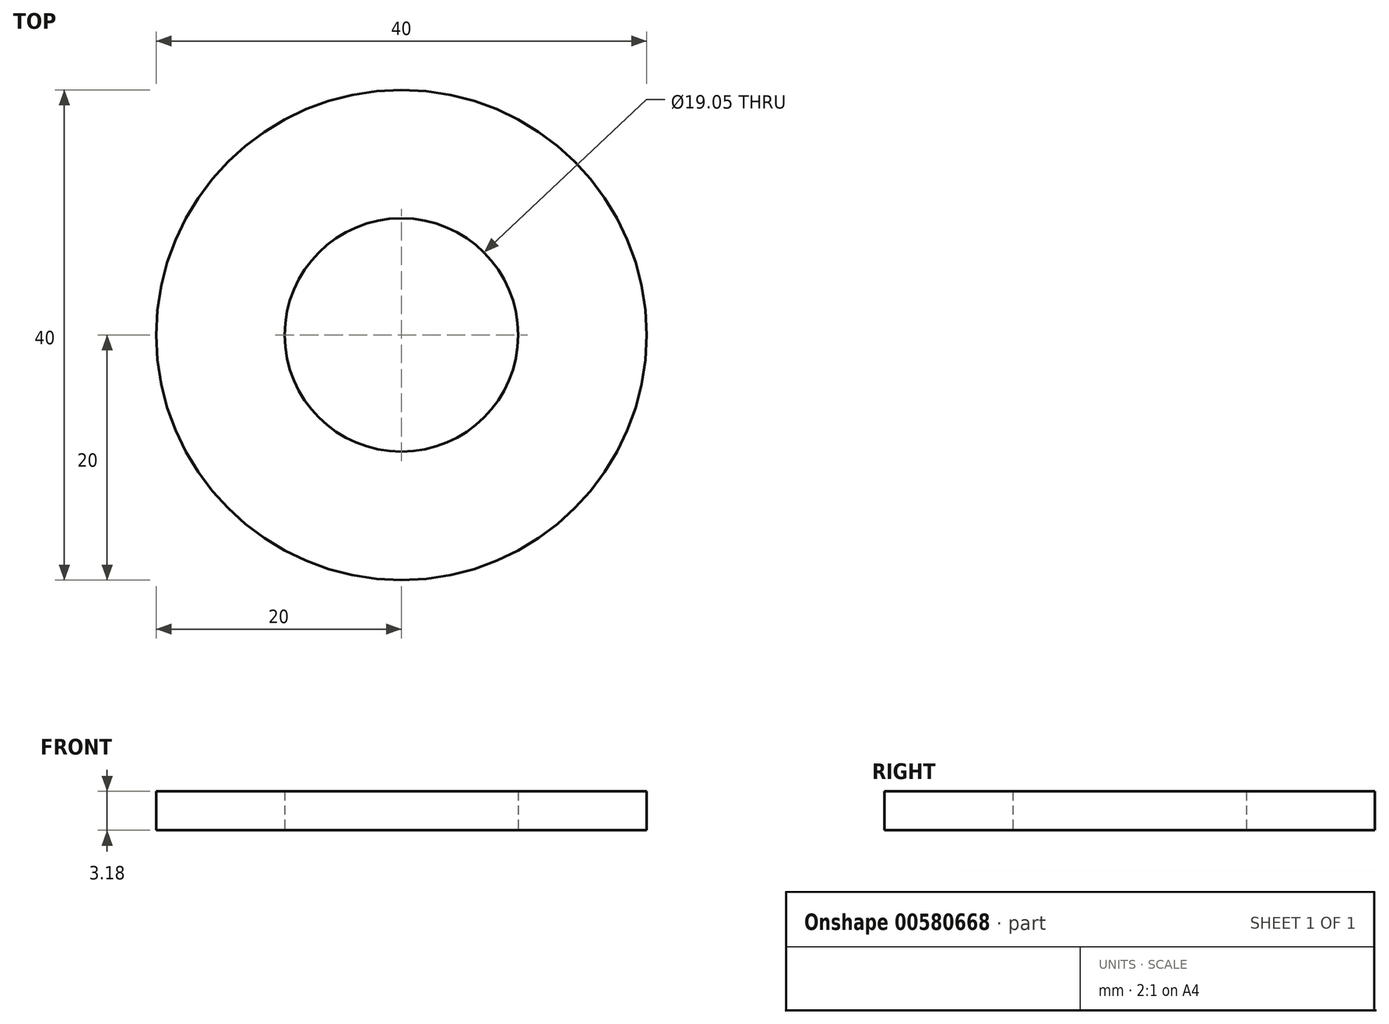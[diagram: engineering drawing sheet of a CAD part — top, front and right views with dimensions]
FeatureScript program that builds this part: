
annotation { "Feature Type Name" : "Feature", "Feature Type Description" : "" }
export const myFeature = defineFeature(function(context is Context, id is Id, definition is map)
    precondition{}
    {
        {
            var Q0;
            Q0=qCreatedBy(makeId("Top.planeOp"),FACE);
            var sketch = newSketch(context, id + "F0", { "sketchPlane" : qUnion([Q0])});
            skCircle(sketch, "E0", {"center": v(0, 0) * mm, "radius": 20 * mm});
            skCircle(sketch, "E1", {"center": v(0, 0) * mm, "radius": 9.53 * mm});
            skSolve(sketch);
        }
        {
            var Q0;
            Q0=makeQuery(id+"F0.imprint","IMPRINT",FACE,{"disambiguationData":[TD([[makeQuery(id+"F0.imprint","IMPRINT",EDGE,{"derivedFrom":sQuery(id+"F0.wireOp",EDGE,"E0")}),1.0]])]});
            extrude(context, id + "F1", {"entities" : qUnion([Q0]), "depth" : 3.17 * mm, "offsetDistance" : 25.4 * mm});
        }
    });
